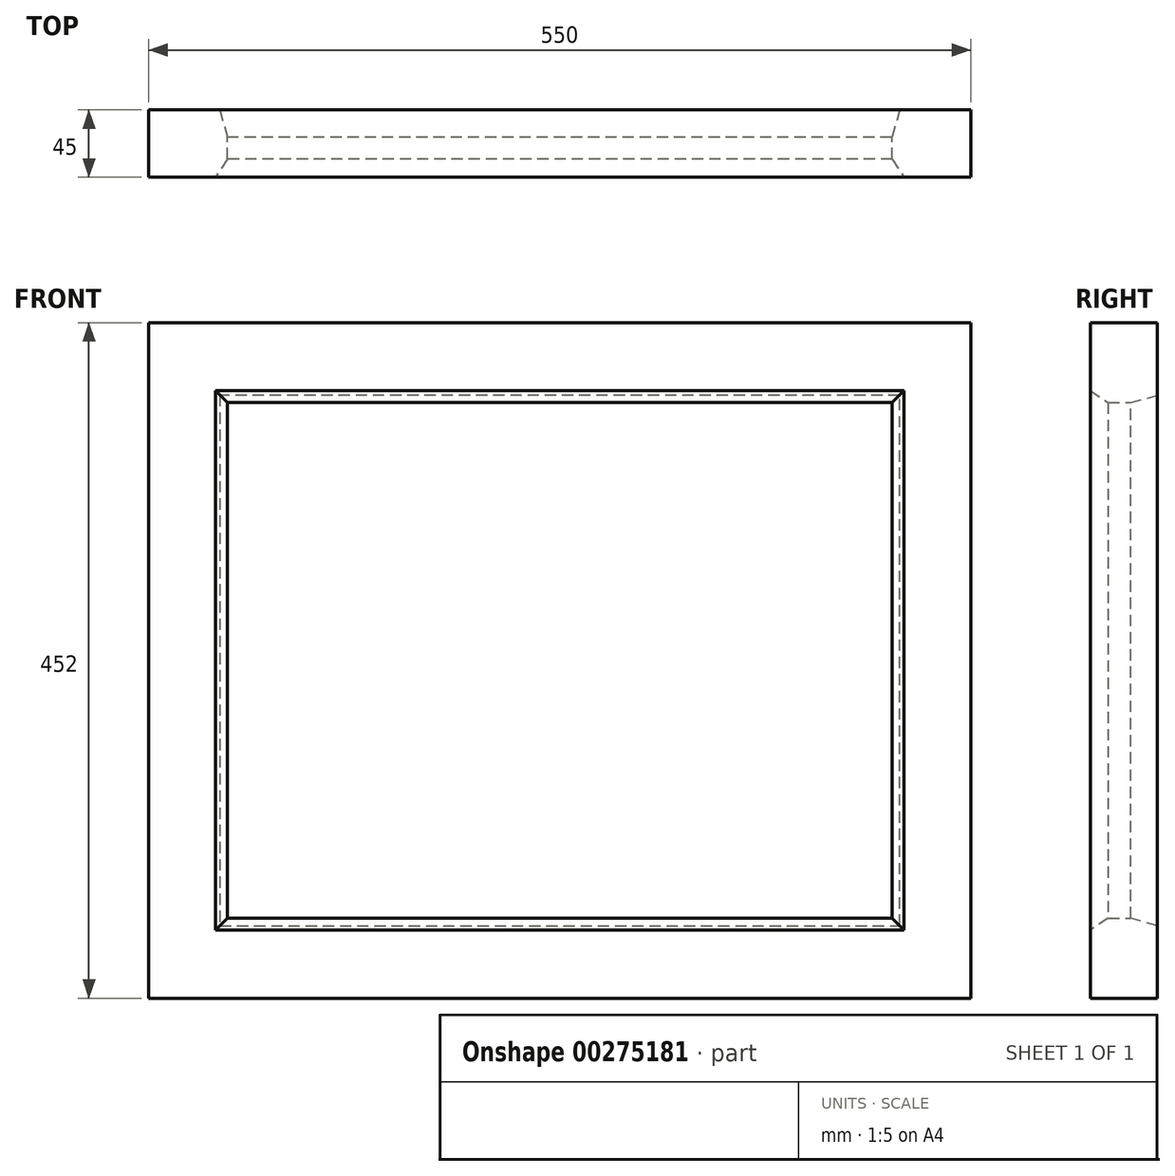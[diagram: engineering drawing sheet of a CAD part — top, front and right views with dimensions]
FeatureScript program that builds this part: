
annotation { "Feature Type Name" : "Feature", "Feature Type Description" : "" }
export const myFeature = defineFeature(function(context is Context, id is Id, definition is map)
    precondition{}
    {
        {
            var Q0;
            Q0=qCreatedBy(makeId("Front.planeOp"),FACE);
            var sketch = newSketch(context, id + "F0", { "sketchPlane" : qUnion([Q0])});
            skLineSegment(sketch, "E0.bottom", {"start": v(-275, 226) * mm, "end": v(275, 226) * mm});
            skLineSegment(sketch, "E0.top", {"start": v(-275, -226) * mm, "end": v(275, -226) * mm});
            skLineSegment(sketch, "E0.left", {"start": v(-275, 226) * mm, "end": v(-275, -226) * mm});
            skLineSegment(sketch, "E0.right", {"start": v(275, 226) * mm, "end": v(275, -226) * mm});
            skPoint(sketch, "E0.middle", {"position": v(0, 0) * mm});
            skLineSegment(sketch, "E1.bottom", {"start": v(-222.5, 172.5) * mm, "end": v(222.5, 172.5) * mm});
            skLineSegment(sketch, "E1.top", {"start": v(-222.5, -172.5) * mm, "end": v(222.5, -172.5) * mm});
            skLineSegment(sketch, "E1.left", {"start": v(-222.5, 172.5) * mm, "end": v(-222.5, -172.5) * mm});
            skLineSegment(sketch, "E1.right", {"start": v(222.5, 172.5) * mm, "end": v(222.5, -172.5) * mm});
            skSolve(sketch);
        }
        {
            var Q0;
            Q0=makeQuery(id+"F0.imprint","IMPRINT",FACE,{"disambiguationData":[TD([[makeQuery(id+"F0.imprint","IMPRINT",EDGE,{"derivedFrom":sQuery(id+"F0.wireOp",EDGE,"E0.bottom")}),-1.0]])]});
            extrude(context, id + "F1", {"entities" : qUnion([Q0]), "endBound" : BoundingType.SYMMETRIC, "depth" : 45 * mm});
        }
        {
            var Q0;
            Q0=makeQuery(id+"F1.opExtrude","CAP_EDGE",EDGE,{"disambiguationData":[OSD([sQuery(id+"F0.wireOp",EDGE,"E1.top")])],"isStart":true});
            var Q1;
            Q1=makeQuery(id+"F1.opExtrude","CAP_EDGE",EDGE,{"disambiguationData":[OSD([sQuery(id+"F0.wireOp",EDGE,"E1.right")])],"isStart":true});
            var Q2;
            Q2=makeQuery(id+"F1.opExtrude","CAP_EDGE",EDGE,{"disambiguationData":[OSD([sQuery(id+"F0.wireOp",EDGE,"E1.left")])],"isStart":true});
            var Q3;
            Q3=makeQuery(id+"F1.opExtrude","CAP_EDGE",EDGE,{"disambiguationData":[OSD([sQuery(id+"F0.wireOp",EDGE,"E1.bottom")])],"isStart":true});
            chamfer(context, id + "F2", {"entities" : qUnion([Q0, Q1, Q2, Q3]), "chamferType" : ChamferType.TWO_OFFSETS, "width1" : 18 * mm, "oppositeDirection" : true, "width2" : 5 * mm, "tangentPropagation" : true});
        }
        {
            var Q0;
            Q0=makeQuery(id+"F1.opExtrude","CAP_EDGE",EDGE,{"disambiguationData":[OSD([sQuery(id+"F0.wireOp",EDGE,"E1.top")])],"isStart":false});
            var Q1;
            Q1=makeQuery(id+"F1.opExtrude","CAP_EDGE",EDGE,{"disambiguationData":[OSD([sQuery(id+"F0.wireOp",EDGE,"E1.left")])],"isStart":false});
            var Q2;
            Q2=makeQuery(id+"F1.opExtrude","CAP_EDGE",EDGE,{"disambiguationData":[OSD([sQuery(id+"F0.wireOp",EDGE,"E1.right")])],"isStart":false});
            var Q3;
            Q3=makeQuery(id+"F1.opExtrude","CAP_EDGE",EDGE,{"disambiguationData":[OSD([sQuery(id+"F0.wireOp",EDGE,"E1.bottom")])],"isStart":false});
            chamfer(context, id + "F3", {"entities" : qUnion([Q0, Q1, Q2, Q3]), "chamferType" : ChamferType.TWO_OFFSETS, "width1" : 8 * mm, "oppositeDirection" : true, "width2" : 12 * mm, "tangentPropagation" : true});
        }
    });
